# Revit family: Building-Materials_Glass-Glazing_Vitro-Architectural-Glass_Azuria-Monolithic-Glass
name_source: partatom
category: Curtain Panels
units: mm (PartAtom-declared; Revit-internal decimal feet)

## family parameters
Always vertical = Yes
Classification Number = 23.25.20.14.11.11.17
Cut with Voids When Loaded = No
Shared = No

## types (1)
- Azuria Monolithic
    Analytic Construction = Large single-glazed windows
    Assembly Code = B2020220
    Define Thermal Properties by = Schematic Type
    Description = Azuria® glass is a stunning aqua-blue glass that is part of the nautically inspired tinted glass collection by Vitro Glass. Azuria® glass’s distinctive aesthetic blends brilliantly with the surrounding environment, adding beauty while delivering solar control and spectrally selective properties that makes it one of the top glasses in the industry.
    Finish = Glass
    Glass Material = Vitro Architectural-Glass - Azuria
    Heat Transfer Coefficient (U) = 0.29 BTU/(h·ft²·°F)
    ISO Damage Weighted Transmittance = 0.651
    Keynote = 08900
    Light to Solar Gain = 1.31
    Manufacturer = Vitro Architectural Glass
    Model = Azuria Monolithic
    Product Guid = 65652ddc-b469-4d42-95d0-bb7b871da1b9
    Product Page URL = https://www.vitroglazings.com
    Product data url = https://www.bimobject.com
    Reflectance (Visible Exterior) = 7
    Reflectance (Visible Interior) = 7
    Shadow Coefficient = 0.6
    Solar Heat Gain Coefficient = 0.52
    Solar Light Transmittance = 0.32
    Thermal Resistance (R) = 8.3333 (h·ft²·°F)/BTU
    Thickness = 0' - 0 1/4"
    U-Value Air (Summer Day) = 0.92 BTU/(h·ft²·°F)
    U-Value Air (Winter Night) = 1.02 BTU/(h·ft²·°F)
    U-Value Argon (Summer Day) = 0 BTU/(h·ft²·°F)
    U-Value Argon (Winter Night) = 0 BTU/(h·ft²·°F)
    URL = https://www.vitroglazings.com
    UV Light Transmittance = 0.42
    Visual Light Transmittance = 0.68

## geometry (parser evidence)
native form markers: Sweep x2
no freeform markers — native parametric forms only
